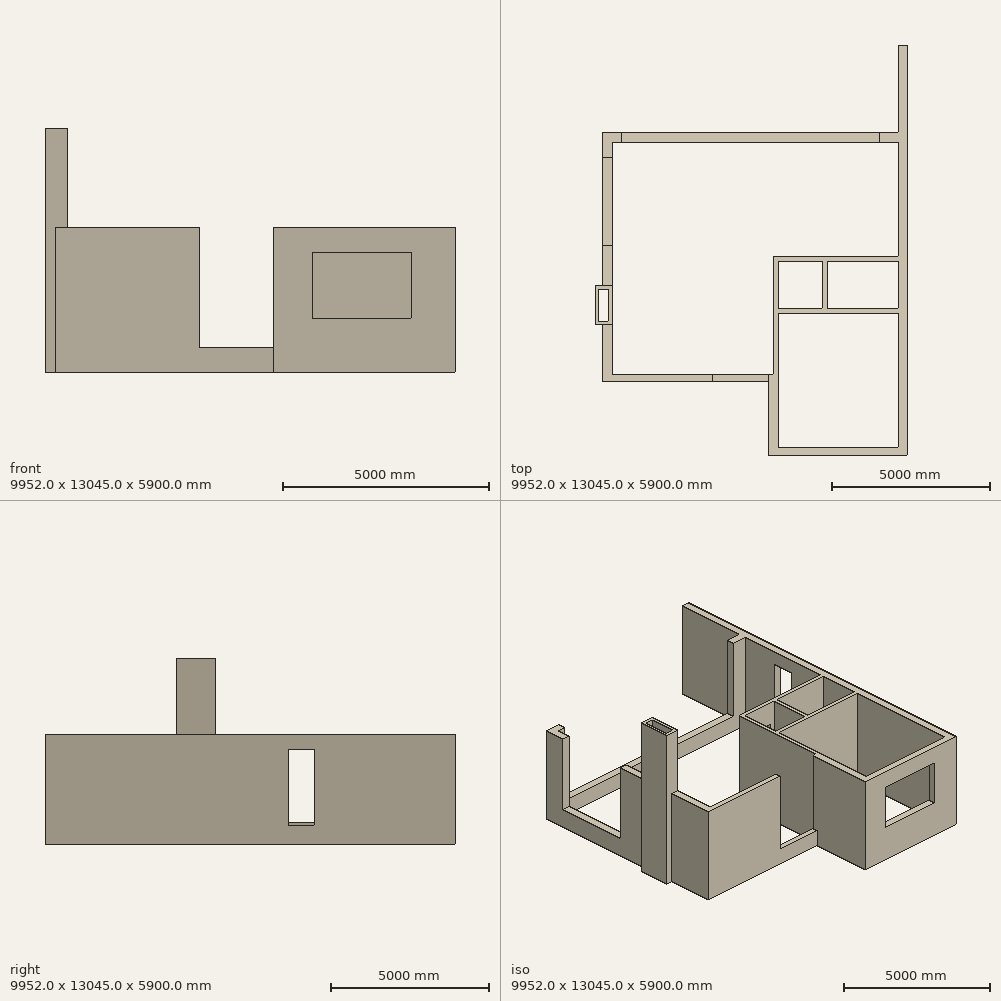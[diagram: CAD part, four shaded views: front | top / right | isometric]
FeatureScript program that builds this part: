
annotation { "Feature Type Name" : "Feature", "Feature Type Description" : "" }
export const myFeature = defineFeature(function(context is Context, id is Id, definition is map)
    precondition{}
    {
        {
            var Q0;
            Q0=qCreatedBy(makeId("Top.planeOp"),FACE);
            var sketch = newSketch(context, id + "F0", { "sketchPlane" : qUnion([Q0])});
            skLineSegment(sketch, "E0", {"start": v(2792.61, 7795.34) * mm, "end": v(2792.61, 9595.34) * mm});
            skLineSegment(sketch, "E1", {"start": v(8084.61, 7795.34) * mm, "end": v(2792.61, 7795.34) * mm});
            skLineSegment(sketch, "E2", {"start": v(9939.61, 10096.34) * mm, "end": v(9939.61, 11605.34) * mm});
            skLineSegment(sketch, "E3", {"start": v(8384.61, 10096.34) * mm, "end": v(9789.61, 10096.34) * mm});
            skLineSegment(sketch, "E4", {"start": v(12504.61, 15699.34) * mm, "end": v(12504.61, 5430.34) * mm});
            skLineSegment(sketch, "E5", {"start": v(12204.61, 10096.34) * mm, "end": v(12204.61, 11605.34) * mm});
            skLineSegment(sketch, "E6", {"start": v(9789.61, 11605.34) * mm, "end": v(9789.61, 10096.34) * mm});
            skLineSegment(sketch, "E7", {"start": v(9939.61, 10096.34) * mm, "end": v(12204.61, 10096.34) * mm});
            skLineSegment(sketch, "E8", {"start": v(3092.61, 7999.34) * mm, "end": v(8234.61, 7999.34) * mm});
            skLineSegment(sketch, "E9", {"start": v(8234.61, 11755.34) * mm, "end": v(12204.61, 11755.34) * mm});
            skLineSegment(sketch, "E10", {"start": v(2792.61, 15699.34) * mm, "end": v(12204.61, 15699.34) * mm});
            skLineSegment(sketch, "E11", {"start": v(12204.61, 11755.34) * mm, "end": v(12204.61, 15399.34) * mm});
            skLineSegment(sketch, "E12", {"start": v(3092.61, 15399.34) * mm, "end": v(12204.61, 15399.34) * mm});
            skLineSegment(sketch, "E13", {"start": v(9939.61, 11605.34) * mm, "end": v(12204.61, 11605.34) * mm});
            skLineSegment(sketch, "E14", {"start": v(3092.61, 15399.34) * mm, "end": v(3092.61, 7999.34) * mm});
            skLineSegment(sketch, "E15", {"start": v(9789.61, 11605.34) * mm, "end": v(8384.61, 11605.34) * mm});
            skLineSegment(sketch, "E16", {"start": v(12504.61, 5430.34) * mm, "end": v(8084.61, 5430.34) * mm});
            skLineSegment(sketch, "E17", {"start": v(8084.61, 5430.34) * mm, "end": v(8084.61, 7795.34) * mm});
            skLineSegment(sketch, "E18", {"start": v(2792.61, 10825.34) * mm, "end": v(2792.61, 15699.34) * mm});
            skLineSegment(sketch, "E19", {"start": v(2792.61, 10825.34) * mm, "end": v(2552.61, 10825.34) * mm});
            skLineSegment(sketch, "E20", {"start": v(2552.61, 10825.34) * mm, "end": v(2552.61, 9595.34) * mm});
            skLineSegment(sketch, "E21", {"start": v(2552.61, 9595.34) * mm, "end": v(2792.61, 9595.34) * mm});
            skLineSegment(sketch, "E22", {"start": v(2662.61, 9705.34) * mm, "end": v(2982.61, 9705.34) * mm});
            skLineSegment(sketch, "E23", {"start": v(2982.61, 9705.34) * mm, "end": v(2982.61, 10715.34) * mm});
            skLineSegment(sketch, "E24", {"start": v(2982.61, 10715.34) * mm, "end": v(2662.61, 10715.34) * mm});
            skLineSegment(sketch, "E25", {"start": v(2662.61, 10715.34) * mm, "end": v(2662.61, 9705.34) * mm});
            skLineSegment(sketch, "E26.bottom", {"start": v(8384.61, 9946.34) * mm, "end": v(12204.61, 9946.34) * mm});
            skLineSegment(sketch, "E26.top", {"start": v(8384.61, 5690.34) * mm, "end": v(12204.61, 5690.34) * mm});
            skLineSegment(sketch, "E26.left", {"start": v(8384.61, 11605.34) * mm, "end": v(8384.61, 10096.34) * mm});
            skLineSegment(sketch, "E26.right", {"start": v(12204.61, 9946.34) * mm, "end": v(12204.61, 5690.34) * mm});
            skLineSegment(sketch, "E27", {"start": v(8234.61, 7999.34) * mm, "end": v(8234.61, 11755.34) * mm});
            skLineSegment(sketch, "E28", {"start": v(6739.61, 7999.34) * mm, "end": v(6739.61, 11931.34) * mm, "construction": true});
            skLineSegment(sketch, "E29", {"start": v(6889.61, 7999.34) * mm, "end": v(6889.61, 12069.34) * mm, "construction": true});
            skLineSegment(sketch, "E30", {"start": v(6889.61, 11931.34) * mm, "end": v(3092.61, 11931.34) * mm, "construction": true});
            skLineSegment(sketch, "E31", {"start": v(6889.61, 12069.34) * mm, "end": v(3092.61, 12069.34) * mm, "construction": true});
            skLineSegment(sketch, "E32", {"start": v(12504.61, 15699.34) * mm, "end": v(12504.61, 18475.34) * mm});
            skLineSegment(sketch, "E33", {"start": v(12204.61, 18475.34) * mm, "end": v(12204.61, 15699.34) * mm});
            skLineSegment(sketch, "E34", {"start": v(2792.61, 15699.34) * mm, "end": v(2792.61, 18225.34) * mm, "construction": true});
            skLineSegment(sketch, "E35", {"start": v(2792.61, 18225.34) * mm, "end": v(12204.61, 18225.34) * mm, "construction": true});
            skLineSegment(sketch, "E36.0", {"start": v(2792.61, 18475.34) * mm, "end": v(12204.61, 18475.34) * mm, "construction": true});
            skLineSegment(sketch, "E37", {"start": v(12204.61, 18475.34) * mm, "end": v(12504.61, 18475.34) * mm});
            skLineSegment(sketch, "E38.trimOffspring", {"start": v(8384.61, 9946.34) * mm, "end": v(8384.61, 5690.34) * mm});
            skLineSegment(sketch, "E39", {"start": v(8084.61, 5430.34) * mm, "end": v(6084.61, 5430.34) * mm, "construction": true});
            skLineSegment(sketch, "E40", {"start": v(6084.61, 5430.34) * mm, "end": v(6084.61, 15699.34) * mm, "construction": true});
            skSolve(sketch);
        }
        {
            var Q0;
            Q0=makeQuery(id+"F0.imprint","IMPRINT",FACE,{"disambiguationData":[TD([[makeQuery(id+"F0.imprint","IMPRINT",EDGE,{"derivedFrom":sQuery(id+"F0.wireOp",EDGE,"E8")}),-1.0]])]});
            var Q1;
            Q1=makeQuery(id+"F0.imprint","IMPRINT",FACE,{"disambiguationData":[TD([[makeQuery(id+"F0.imprint","IMPRINT",EDGE,{"derivedFrom":sQuery(id+"F0.wireOp",EDGE,"E2")}),1.0]])]});
            extrude(context, id + "F1", {"entities" : qUnion([Q0, Q1]), "depth" : 2900 * mm, "offsetDistance" : 25 * mm, "hasSecondDirection" : true, "secondDirectionOppositeDirection" : true, "secondDirectionDepth" : 600 * mm});
        }
        {
            var Q0;
            Q0=makeQuery(id+"F1.opExtrude","CAP_FACE",FACE,{"disambiguationData":[OSD([sQuery(id+"F0.wireOp",EDGE,"E0"),sQuery(id+"F0.wireOp",EDGE,"E8"),sQuery(id+"F0.wireOp",EDGE,"E14"),sQuery(id+"F0.wireOp",EDGE,"ffccaf59-bd0e-409d-86e8-2928bd15204e"),sQuery(id+"F0.wireOp",EDGE,"1befd5c3-4ccf-4a88-a599-4b3555715230"),sQuery(id+"F0.wireOp",EDGE,"d12e0f0d-a76b-486d-91e4-0784727cf8f8"),sQuery(id+"F0.wireOp",EDGE,"643ffdcd-3554-4d6c-aa3c-f980cf73695a"),sQuery(id+"F0.wireOp",EDGE,"b4218357-168d-4a43-a74e-ee97c6fa0a81"),sQuery(id+"F0.wireOp",EDGE,"9507bca5-91be-4127-85b7-07d1a660f050"),sQuery(id+"F0.wireOp",EDGE,"bcf94ef9-d6fc-4982-bc2a-73e3dd7114b1"),sQuery(id+"F0.wireOp",EDGE,"bf902b1c-fc11-4e6c-b5f3-1f7c398e48fe"),sQuery(id+"F0.wireOp",EDGE,"E18"),sQuery(id+"F0.wireOp",EDGE,"e5a2760d-cd0e-47f8-87c7-826fa4ff6e49"),sQuery(id+"F0.wireOp",EDGE,"E19"),sQuery(id+"F0.wireOp",EDGE,"E20"),sQuery(id+"F0.wireOp",EDGE,"E21"),sQuery(id+"F0.wireOp",EDGE,"E22"),sQuery(id+"F0.wireOp",EDGE,"E23"),sQuery(id+"F0.wireOp",EDGE,"E24"),sQuery(id+"F0.wireOp",EDGE,"E25")])],"isStart":false});
            var sketch = newSketch(context, id + "F2", { "sketchPlane" : qUnion([Q0])});
            skLineSegment(sketch, "E41.bottom", {"start": v(3092.61, 10825.34) * mm, "end": v(2552.61, 10825.34) * mm});
            skLineSegment(sketch, "E41.top", {"start": v(3092.61, 9595.34) * mm, "end": v(2552.61, 9595.34) * mm});
            skLineSegment(sketch, "E41.left", {"start": v(3092.61, 10825.34) * mm, "end": v(3092.61, 9595.34) * mm});
            skLineSegment(sketch, "E41.right", {"start": v(2552.61, 10825.34) * mm, "end": v(2552.61, 9595.34) * mm});
            skLineSegment(sketch, "E42.bottom", {"start": v(2982.61, 10715.34) * mm, "end": v(2662.61, 10715.34) * mm});
            skLineSegment(sketch, "E42.top", {"start": v(2982.61, 9705.34) * mm, "end": v(2662.61, 9705.34) * mm});
            skLineSegment(sketch, "E42.left", {"start": v(2982.61, 10715.34) * mm, "end": v(2982.61, 9705.34) * mm});
            skLineSegment(sketch, "E42.right", {"start": v(2662.61, 10715.34) * mm, "end": v(2662.61, 9705.34) * mm});
            skSolve(sketch);
        }
        {
            var Q0;
            {var subQ4=sQuery(id+"F2.wireOp",EDGE,"E41.right");Q0=makeQuery(id+"F2.imprint","IMPRINT",FACE,{"disambiguationData":[TD([[makeQuery(id+"F2.imprint","IMPRINT",EDGE,{"derivedFrom":subQ4}),1.0]])]});}
            extrude(context, id + "F3", {"entities" : qUnion([Q0]), "operationType" : NewBodyOperationType.ADD, "depth" : 2400 * mm, "offsetDistance" : 25 * mm});
        }
        {
            var Q0;
            Q0=makeQuery(id+"F1.opExtrude","SWEPT_FACE",FACE,{"disambiguationData":[OSD([sQuery(id+"F0.wireOp",EDGE,"E11"),sQuery(id+"F0.wireOp",EDGE,"57610e16-034d-4030-9863-af1c284f2f90")])]});
            var sketch = newSketch(context, id + "F4", { "sketchPlane" : qUnion([Q0])});
            skLineSegment(sketch, "E43.bottom", {"start": v(-13986.84, 0) * mm, "end": v(-13166.84, 0) * mm});
            skLineSegment(sketch, "E43.top", {"start": v(-13986.84, 2400) * mm, "end": v(-13166.84, 2400) * mm});
            skLineSegment(sketch, "E43.left", {"start": v(-13986.84, 0) * mm, "end": v(-13986.84, 2400) * mm});
            skLineSegment(sketch, "E43.right", {"start": v(-13166.84, 0) * mm, "end": v(-13166.84, 2400) * mm});
            skSolve(sketch);
        }
        {
            var Q0;
            Q0=makeQuery(id+"F4.imprint","IMPRINT",FACE,{"disambiguationData":[TD([[makeQuery(id+"F4.imprint","IMPRINT",EDGE,{"derivedFrom":sQuery(id+"F4.wireOp",EDGE,"E43.bottom")}),1.0]])]});
            extrude(context, id + "F5", {"entities" : qUnion([Q0]), "operationType" : NewBodyOperationType.REMOVE, "endBound" : BoundingType.UP_TO_NEXT, "oppositeDirection" : true, "depth" : 25 * mm, "offsetDistance" : 25 * mm});
        }
        {
            var Q0;
            Q0=makeQuery(id+"F1.opExtrude","SWEPT_FACE",FACE,{"disambiguationData":[OSD([sQuery(id+"F0.wireOp",EDGE,"E16")])]});
            var sketch = newSketch(context, id + "F6", { "sketchPlane" : qUnion([Q0])});
            skLineSegment(sketch, "E44.bottom", {"start": v(9041.61, 2300) * mm, "end": v(11441.61, 2300) * mm});
            skLineSegment(sketch, "E44.top", {"start": v(9041.61, 700) * mm, "end": v(11441.61, 700) * mm});
            skLineSegment(sketch, "E44.left", {"start": v(9041.61, 2300) * mm, "end": v(9041.61, 700) * mm});
            skLineSegment(sketch, "E44.right", {"start": v(11441.61, 2300) * mm, "end": v(11441.61, 700) * mm});
            skSolve(sketch);
        }
        {
            var Q0;
            Q0=makeQuery(id+"F6.imprint","IMPRINT",FACE,{"disambiguationData":[TD([[makeQuery(id+"F6.imprint","IMPRINT",EDGE,{"derivedFrom":sQuery(id+"F6.wireOp",EDGE,"E44.bottom")}),-1.0]])]});
            extrude(context, id + "F7", {"entities" : qUnion([Q0]), "operationType" : NewBodyOperationType.REMOVE, "endBound" : BoundingType.UP_TO_NEXT, "oppositeDirection" : true, "depth" : 25 * mm, "offsetDistance" : 25 * mm});
        }
        {
            var Q0;
            Q0=makeQuery(id+"FNkTqrfbGedaEju_7.boolean.opBoolean","MERGE",FACE,{"derivedFrom":[makeQuery(id+"F1.opExtrude","SWEPT_FACE",FACE,{"disambiguationData":[OSD([sQuery(id+"F0.wireOp",EDGE,"E9")])]}),makeQuery(id+"FNkTqrfbGedaEju_7.opExtrude","SWEPT_FACE",FACE,{"disambiguationData":[OSD([sQuery(id+"FuzePkwGuleFcN0_7.wireOp",EDGE,"k6JzSxQF-srIe-5VRv-kDIz-fuSQgqntkGs6.left")])]})]});
            var sketch = newSketch(context, id + "F8", { "sketchPlane" : qUnion([Q0])});
            skLineSegment(sketch, "E45.bottom", {"start": v(-9610.61, 0) * mm, "end": v(-8790.61, 0) * mm});
            skLineSegment(sketch, "E45.top", {"start": v(-9610.61, 2040) * mm, "end": v(-8790.61, 2040) * mm});
            skLineSegment(sketch, "E45.left", {"start": v(-9610.61, 0) * mm, "end": v(-9610.61, 2040) * mm});
            skLineSegment(sketch, "E45.right", {"start": v(-8790.61, 0) * mm, "end": v(-8790.61, 2040) * mm});
            skSolve(sketch);
        }
        {
            var Q0;
            Q0=makeQuery(id+"F8.imprint","IMPRINT",FACE,{"disambiguationData":[TD([[makeQuery(id+"F8.imprint","IMPRINT",EDGE,{"derivedFrom":sQuery(id+"F8.wireOp",EDGE,"E45.bottom")}),1.0]])]});
            extrude(context, id + "F9", {"entities" : qUnion([Q0]), "operationType" : NewBodyOperationType.REMOVE, "endBound" : BoundingType.UP_TO_NEXT, "oppositeDirection" : true, "depth" : 25 * mm, "offsetDistance" : 25 * mm});
        }
        {
            var Q0;
            Q0=makeQuery(id+"F1.opExtrude","SWEPT_FACE",FACE,{"disambiguationData":[OSD([sQuery(id+"F0.wireOp",EDGE,"E18")])]});
            var sketch = newSketch(context, id + "F10", { "sketchPlane" : qUnion([Q0])});
            skLineSegment(sketch, "E46.bottom", {"start": v(-14899.34, 100) * mm, "end": v(-12099.34, 100) * mm});
            skLineSegment(sketch, "E46.top", {"start": v(-14899.34, 2900) * mm, "end": v(-12099.34, 2900) * mm});
            skLineSegment(sketch, "E46.left", {"start": v(-14899.34, 100) * mm, "end": v(-14899.34, 2900) * mm});
            skLineSegment(sketch, "E46.right", {"start": v(-12099.34, 100) * mm, "end": v(-12099.34, 2900) * mm});
            skSolve(sketch);
        }
        {
            var Q0;
            Q0 = qSketchRegion(id + "F10", true);
            extrude(context, id + "F11", {"entities" : qUnion([Q0]), "operationType" : NewBodyOperationType.REMOVE, "endBound" : BoundingType.UP_TO_NEXT, "oppositeDirection" : true, "depth" : 25 * mm, "offsetDistance" : 25 * mm});
        }
        {
            var Q0;
            Q0=makeQuery(id+"F1.opExtrude","SWEPT_FACE",FACE,{"disambiguationData":[OSD([sQuery(id+"F0.wireOp",EDGE,"E10")])]});
            var sketch = newSketch(context, id + "F12", { "sketchPlane" : qUnion([Q0])});
            skLineSegment(sketch, "E47.bottom", {"start": v(-11604.61, 2900) * mm, "end": v(-3392.61, 2900) * mm});
            skLineSegment(sketch, "E47.top", {"start": v(-11604.61, 0) * mm, "end": v(-3392.61, 0) * mm});
            skLineSegment(sketch, "E47.left", {"start": v(-11604.61, 0) * mm, "end": v(-11604.61, 2900) * mm});
            skLineSegment(sketch, "E47.right", {"start": v(-3392.61, 0) * mm, "end": v(-3392.61, 2900) * mm});
            skSolve(sketch);
        }
        {
            var Q0;
            Q0=makeQuery(id+"F12.imprint","IMPRINT",FACE,{"disambiguationData":[TD([[makeQuery(id+"F12.imprint","IMPRINT",EDGE,{"derivedFrom":sQuery(id+"F12.wireOp",EDGE,"E47.bottom")}),1.0]])]});
            extrude(context, id + "F13", {"entities" : qUnion([Q0]), "operationType" : NewBodyOperationType.REMOVE, "endBound" : BoundingType.UP_TO_NEXT, "oppositeDirection" : true, "depth" : 25 * mm, "offsetDistance" : 25 * mm});
        }
        {
            var Q0;
            Q0=makeQuery(id+"F1.opExtrude","SWEPT_FACE",FACE,{"disambiguationData":[OSD([sQuery(id+"F0.wireOp",EDGE,"E1")])]});
            var sketch = newSketch(context, id + "F14", { "sketchPlane" : qUnion([Q0])});
            skLineSegment(sketch, "E48.bottom", {"start": v(8084.61, 2900) * mm, "end": v(6284.61, 2900) * mm});
            skLineSegment(sketch, "E48.top", {"start": v(8084.61, 0) * mm, "end": v(6284.61, 0) * mm});
            skLineSegment(sketch, "E48.left", {"start": v(8084.61, 2900) * mm, "end": v(8084.61, 0) * mm});
            skLineSegment(sketch, "E48.right", {"start": v(6284.61, 2900) * mm, "end": v(6284.61, 0) * mm});
            skSolve(sketch);
        }
        {
            var Q0;
            Q0=makeQuery(id+"F14.imprint","IMPRINT",FACE,{"disambiguationData":[TD([[makeQuery(id+"F14.imprint","IMPRINT",EDGE,{"derivedFrom":sQuery(id+"F14.wireOp",EDGE,"E48.bottom")}),1.0]])]});
            extrude(context, id + "F15", {"entities" : qUnion([Q0]), "operationType" : NewBodyOperationType.REMOVE, "endBound" : BoundingType.UP_TO_NEXT, "oppositeDirection" : true, "depth" : 25 * mm, "offsetDistance" : 25 * mm});
        }
    });
